# Revit family: Flush_Valve-Toilet-American_Standard-Ultima_Sensor-6147SM16X_Series
name_source: partatom
category: Plumbing Fixtures
units: mm (PartAtom-declared; Revit-internal decimal feet)

## family parameters
Always vertical = No
Cut with Voids When Loaded = No
OmniClass Number = 23.65.70.00
OmniClass Title = Terminals for Supplied Liquids and Gases
Part Type = Normal
Room Calculation Point = No
Round Connector Dimension = Use Diameter
Shared = Yes
Work Plane-Based = Yes

## types (2) — shared parameters
ADA Compliant = Yes
Assembly Code = D2020100
CW Connection = Yes
CWFU = 10
Cold Water Connection Diameter = 1"
Cold Water Connection Radius = 1/2"
Connection Distance = 11 1/2"
Default Elevation = 0"
Description = Ultima Sensor-Operated Toilet Flush Valve Diaphragm-Type
Finish = Brass-American Standard-002-Polished Chrome
Flush Rate = 1.6 gpf (6.0 Lpf)
HW Connection = No
Installation Type = Top Spud
Manufacturer = American Standard
Material = Brass-American Standard-002-Polished Chrome
Operating Pressure = 25 psi (flowing) - 80 psi (static)
Price = Prices may vary. Please consult Manufacturer Representative for most up-to-date price list.
Product Documentation Link = https://americanstandard.box.com
Product Page URL = https://www.americanstandard-us.com
Revised Date = 09/30/2021
URL = https://www.americanstandard-us.com
Vent Connection = No
Warranty Information = 1 Year Limited Warranty
Waste Connection = No
zero-valued in all types: HWFU, WFU

## per-type parameters (varying)
| type | Center to Wall | Center to Wall Constraint | Cold Water Connection Height | Cold Water Connection Width | Cold Water Connection Width Constraint | Height |
| 6147SM161.002 | 5" | 5" | 11 1/2" | 5 1/4" | 6" | 14 5/8" |
| 6147SM162.002 | 1 1/2" | 1" | 27" | 4 1/4" | 2" | 30 1/8" |

note: column(s) folded — value = type name in every type: Model

## geometry (parser evidence)
native form markers: Sweep x2
no freeform markers — native parametric forms only
